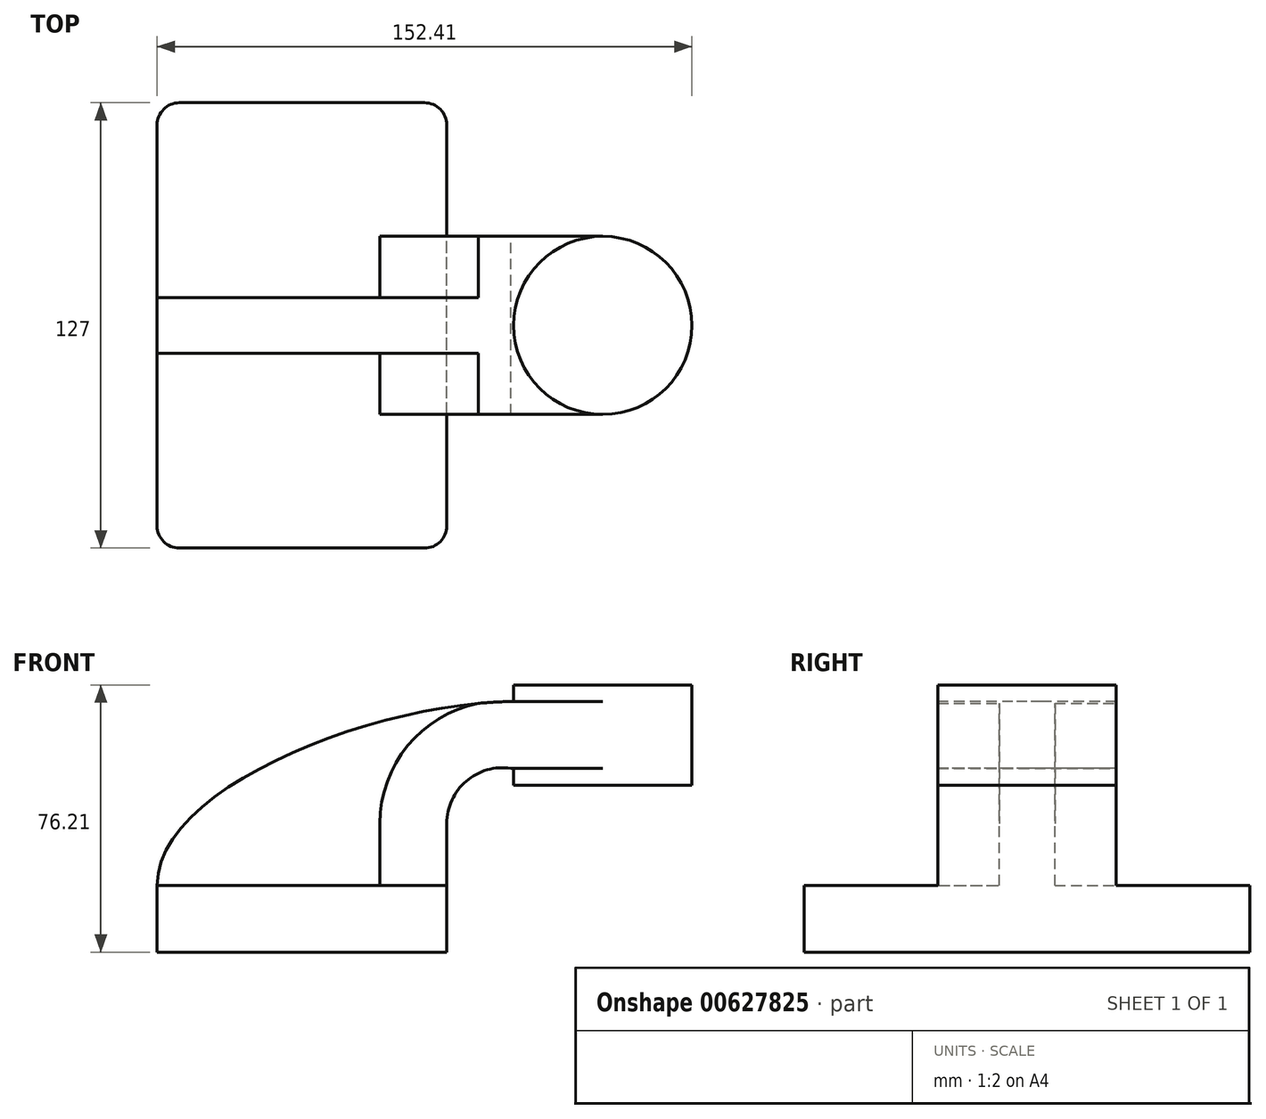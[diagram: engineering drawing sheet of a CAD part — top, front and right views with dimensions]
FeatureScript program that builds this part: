
annotation { "Feature Type Name" : "Feature", "Feature Type Description" : "" }
export const myFeature = defineFeature(function(context is Context, id is Id, definition is map)
    precondition{}
    {
        {
            var Q0;
            Q0=qCreatedBy(makeId("Front.planeOp"),FACE);
            var sketch = newSketch(context, id + "F0", { "sketchPlane" : qUnion([Q0])});
            skLineSegment(sketch, "E0.bottom", {"start": v(-41.28, 9.52) * mm, "end": v(41.27, 9.53) * mm});
            skLineSegment(sketch, "E0.top", {"start": v(-41.28, -9.53) * mm, "end": v(41.28, -9.53) * mm});
            skLineSegment(sketch, "E0.left", {"start": v(-41.28, 9.52) * mm, "end": v(-41.28, -9.53) * mm});
            skLineSegment(sketch, "E0.right", {"start": v(41.27, 9.53) * mm, "end": v(41.28, -9.52) * mm});
            skPoint(sketch, "E0.middle", {"position": v(0, 0) * mm});
            skLineSegment(sketch, "E1.bottom", {"start": v(60.32, 38.1) * mm, "end": v(111.12, 38.1) * mm});
            skLineSegment(sketch, "E1.top", {"start": v(60.32, 66.68) * mm, "end": v(111.12, 66.68) * mm});
            skLineSegment(sketch, "E1.left", {"start": v(60.32, 38.1) * mm, "end": v(60.32, 66.67) * mm});
            skLineSegment(sketch, "E1.right", {"start": v(111.12, 38.1) * mm, "end": v(111.12, 66.68) * mm});
            skPoint(sketch, "E1.middle", {"position": v(85.72, 52.39) * mm});
            skLineSegment(sketch, "E2", {"start": v(41.27, 9.53) * mm, "end": v(41.27, 27.18) * mm});
            skArc(sketch, "E3", {"start": v(41.27, 27.18) * mm, "mid": v(46.8, 39.2) * mm, "end": v(59.5, 42.88) * mm});
            skLineSegment(sketch, "E4", {"start": v(59.5, 42.88) * mm, "end": v(85.72, 42.88) * mm});
            skLineSegment(sketch, "E5.0", {"start": v(60.65, 61.93) * mm, "end": v(85.72, 61.93) * mm});
            skArc(sketch, "E5.1", {"start": v(22.22, 27.18) * mm, "mid": v(33.72, 53.08) * mm, "end": v(60.65, 61.93) * mm});
            skLineSegment(sketch, "E5.2", {"start": v(22.22, 9.53) * mm, "end": v(22.22, 27.18) * mm});
            skLineSegment(sketch, "E6", {"start": v(85.72, 38.1) * mm, "end": v(85.72, 66.68) * mm});
            skFitSpline(sketch, "E7", {"points": [v(-41.27, 9.53) * mm, v(60.65, 61.93) * mm], "startDerivative": vector(0, 85.73) * mm, "endDerivative": vector(115.28, 0) * mm});
            skSolve(sketch);
        }
        {
            var Q0;
            Q0=makeQuery(id+"F0.imprint","IMPRINT",FACE,{"disambiguationData":[TD([[makeQuery(id+"F0.imprint","IMPRINT",EDGE,{"derivedFrom":sQuery(id+"F0.wireOp",EDGE,"E0.top")}),1.0]])]});
            extrude(context, id + "F1", {"entities" : qUnion([Q0]), "endBound" : BoundingType.SYMMETRIC, "depth" : 127 * mm, "offsetDistance" : 25.4 * mm});
        }
        {
            var Q0;
            {var subQ0=sQuery(id+"F0.wireOp",EDGE,"E2");Q0=makeQuery(id+"F0.imprint","IMPRINT",FACE,{"disambiguationData":[TD([[makeQuery(id+"F0.imprint","IMPRINT",EDGE,{"derivedFrom":subQ0}),1.0]])]});}
            var Q1;
            {var subQ3=sQuery(id+"F0.wireOp",EDGE,"E5.0");Q1=makeQuery(id+"F0.imprint","IMPRINT",FACE,{"disambiguationData":[TD([[makeQuery(id+"F0.imprint","IMPRINT",EDGE,{"derivedFrom":subQ3}),-1.0]])]});}
            extrude(context, id + "F2", {"entities" : qUnion([Q0, Q1]), "operationType" : NewBodyOperationType.ADD, "endBound" : BoundingType.SYMMETRIC, "depth" : 50.8 * mm, "offsetDistance" : 25.4 * mm});
        }
        {
            var Q0;
            {var subQ3=sQuery(id+"F0.wireOp",EDGE,"E5.2");Q0=makeQuery(id+"F0.imprint","IMPRINT",FACE,{"disambiguationData":[TD([[makeQuery(id+"F0.imprint","IMPRINT",EDGE,{"derivedFrom":subQ3}),1.0]])]});}
            extrude(context, id + "F3", {"entities" : qUnion([Q0]), "operationType" : NewBodyOperationType.ADD, "endBound" : BoundingType.SYMMETRIC, "depth" : 15.88 * mm, "offsetDistance" : 25.4 * mm});
        }
        {
            var Q0;
            {var subQ4=sQuery(id+"F0.wireOp",EDGE,"E1.right");Q0=makeQuery(id+"F0.imprint","IMPRINT",FACE,{"disambiguationData":[TD([[makeQuery(id+"F0.imprint","IMPRINT",EDGE,{"derivedFrom":subQ4}),1.0]])]});}
            var Q1;
            Q1=sQuery(id+"F0.wireOp",EDGE,"E6");
            revolve(context, id + "F4", {"operationType" : NewBodyOperationType.ADD, "entities" : qUnion([Q0]), "axis" : qUnion([Q1]), "revolveType" : RevolveType.FULL});
        }
        {
            var Q0;
            Q0=makeQuery(id+"F1.opExtrude","CAP_EDGE",EDGE,{"disambiguationData":[OSD([sQuery(id+"F0.wireOp",EDGE,"E0.right")])],"isStart":false});
            var Q1;
            Q1=makeQuery(id+"F1.opExtrude","CAP_EDGE",EDGE,{"disambiguationData":[OSD([sQuery(id+"F0.wireOp",EDGE,"E0.left")])],"isStart":false});
            var Q2;
            Q2=makeQuery(id+"F1.opExtrude","CAP_EDGE",EDGE,{"disambiguationData":[OSD([sQuery(id+"F0.wireOp",EDGE,"E0.right")])],"isStart":true});
            var Q3;
            Q3=makeQuery(id+"F1.opExtrude","CAP_EDGE",EDGE,{"disambiguationData":[OSD([sQuery(id+"F0.wireOp",EDGE,"E0.left")])],"isStart":true});
            fillet(context, id + "F5", {"entities" : qUnion([Q0, Q1, Q2, Q3]), "radius" : 6.35 * mm, "tangentPropagation" : true, "allowEdgeOverflow" : false});
        }
    });
